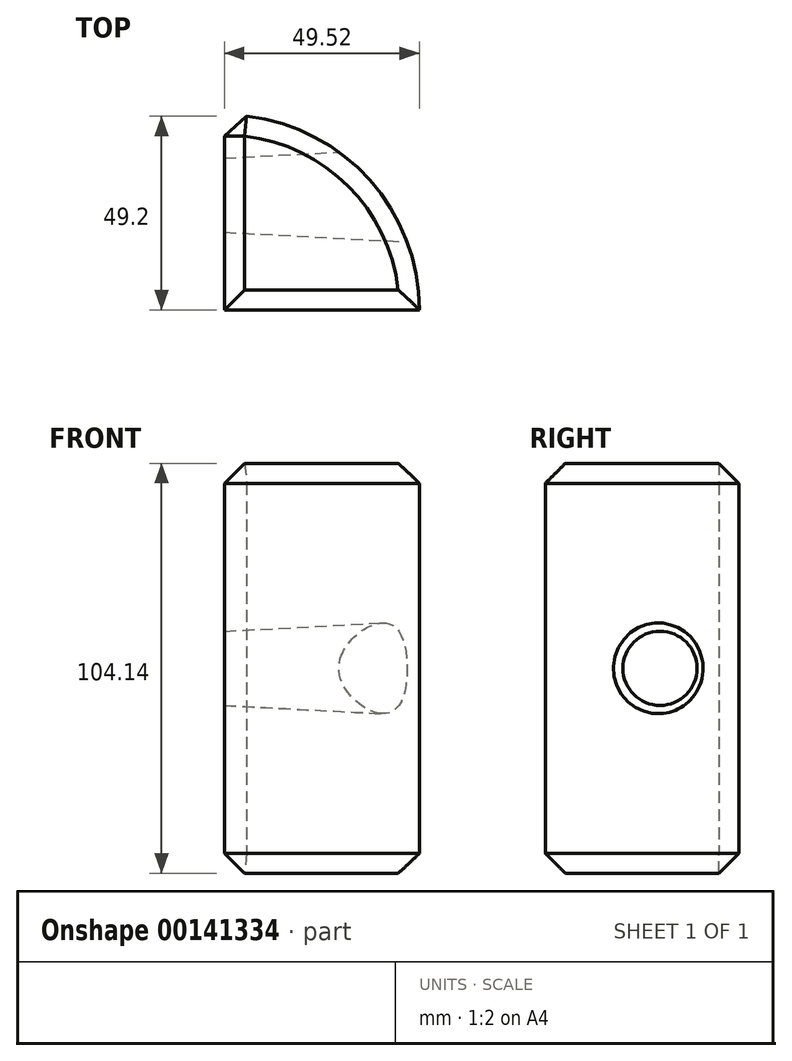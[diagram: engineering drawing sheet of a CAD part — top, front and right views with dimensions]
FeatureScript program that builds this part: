
annotation { "Feature Type Name" : "Feature", "Feature Type Description" : "" }
export const myFeature = defineFeature(function(context is Context, id is Id, definition is map)
    precondition{}
    {
        {
            var Q0;
            Q0=qCreatedBy(makeId("Top.planeOp"),FACE);
            var sketch = newSketch(context, id + "F0", { "sketchPlane" : qUnion([Q0])});
            skLineSegment(sketch, "E0.bottom", {"start": v(0, 0) * mm, "end": v(49.52, 0) * mm});
            skLineSegment(sketch, "E0.top", {"start": v(0, 49.52) * mm, "end": v(0, 49.52) * mm});
            skLineSegment(sketch, "E0.left", {"start": v(0, 0) * mm, "end": v(0, 49.52) * mm});
            skArc(sketch, "E1", {"start": v(49.52, 0) * mm, "mid": v(35.02, 35.02) * mm, "end": v(0, 49.52) * mm});
            skSolve(sketch);
        }
        {
            var Q0;
            Q0 = qSketchRegion(id + "F0", true);
            extrude(context, id + "F1", {"entities" : qUnion([Q0]), "depth" : 104.14 * mm, "symmetric" : true});
        }
        {
            var Q0;
            Q0=makeQuery(id+"F1.opExtrude","SWEPT_EDGE",EDGE,{"disambiguationData":[OSD([sQuery(id+"F0.wireOp",EDGE,"E0.left"),sQuery(id+"F0.wireOp",EDGE,"E1")])]});
            var Q1;
            Q1=makeQuery(id+"F1.opExtrude","CAP_EDGE",EDGE,{"disambiguationData":[OSD([sQuery(id+"F0.wireOp",EDGE,"E0.left")])],"isStart":false});
            var Q2;
            Q2=makeQuery(id+"F1.opExtrude","CAP_EDGE",EDGE,{"disambiguationData":[OSD([sQuery(id+"F0.wireOp",EDGE,"E1")])],"isStart":false});
            var Q3;
            Q3=makeQuery(id+"F1.opExtrude","CAP_EDGE",EDGE,{"disambiguationData":[OSD([sQuery(id+"F0.wireOp",EDGE,"E0.bottom")])],"isStart":false});
            var Q4;
            Q4=makeQuery(id+"F1.opExtrude","CAP_FACE",FACE,{"disambiguationData":[OSD([sQuery(id+"F0.wireOp",EDGE,"E0.bottom"),sQuery(id+"F0.wireOp",EDGE,"E0.left"),sQuery(id+"F0.wireOp",EDGE,"E1")])],"isStart":true});
            chamfer(context, id + "F2", {"entities" : qUnion([Q0, Q1, Q2, Q3, Q4]), "width" : 5.08 * mm, "tangentPropagation" : true});
        }
        {
            var Q0;
            Q0=qCreatedBy(makeId("Right.planeOp"),FACE);
            var sketch = newSketch(context, id + "F3", { "sketchPlane" : qUnion([Q0])});
            skCircle(sketch, "E2", {"center": v(29.14, 0) * mm, "radius": 9.42 * mm});
            skSolve(sketch);
        }
        {
            var Q0;
            Q0 = qSketchRegion(id + "F3", true);
            extrude(context, id + "F4", {"entities" : qUnion([Q0]), "operationType" : NewBodyOperationType.REMOVE, "endBound" : BoundingType.THROUGH_ALL, "depth" : 25.4 * mm, "hasDraft" : true, "draftAngle" : 3 * degree});
        }
    });
